# Revit family: P550083-031
name_source: partatom
category: Lighting Fixtures
units: mm (PartAtom-declared; Revit-internal decimal feet)

## family parameters
Cut with Voids When Loaded = No
Host = Face
Light Source = Yes
OmniClass Number = 23.80.70.11.14.17
OmniClass Title = Direct/Indirect
Part Type = Normal
Room Calculation Point = No
Round Connector Dimension = Use Diameter
Shared = Yes

## types (1)
- P550083-031
    Apparent Load = 60 VA
    Assembly Code = D5020200
    Color Filter = 16777215
    Connector Description = Lighting Connector
    Default Elevation = 48 "
    Description = Pawley Collection One-Light Matte Black and Dark Gray Rattan Indoor/Outdoor Hanging Pendant Light
    Dimming Lamp Color Temperature Shift = <None>
    Features = Application: Unite global feel and coastal warmth with the Pawley Collection 1-Light Dark Gray Rattan Coastal Outdoor Hanging Pendant Light ideal for any hallway, stairwell, entryway, kitchen, sitting room, covered patio, or porch.
Styles: Perfect for coastal, global, and transitional style settings.
Finish: The synthetic dark gray rattan frame has a graceful, lattice-like design that gives the fixture charm and depth.
Materials: Constructed from steel to ensure a long product lifespan.
Glass/Shades: A light source diffuses from within the etched glass shade cradled inside the airy basketweave design offering an organic feel.
Bulbs: For ideal illumination, use 1 medium base bulb that is sold separately (100w max - LED/CFL/incandescent). Compatible with dimmable bulbs.
Dimensions: Measures 12-inch diameter by 16-inch height.
Certifications: cETLus damp location listed.
Pairs With: Pairs with a variety of Progress Lighting fixtures.
Warranty: Our 1-Year Limited Warranty guarantees your complete satisfaction with your purchase and includes professional after-sales customer service support.
    Fixture distribution = Direct
    Glass = Paint - Hubbell - White Texture
    Gold = Hubbell - Gold
    Housing Material = Paint - Hubbell - Textured Camera Black
    Lamp = LED/CFL/incandescent
    Load Classification = Lighting
    Manufacturer = Progress Lighting
    Model = P550083-031
    Photometric Web File = generic
    Power Factor = 1
    Product Documentation Link = https://hubbellcdn.com
    Product Link = https://www.hubbell.com
    Tilt Angle = -90.00°
    URL = https://www.hubbell.com
    Voltage = 120 V
    Warranty = 1 year Warranty
    Wattage Comments = 60W
    Watts = 60 W
    Wood = Hubbell - Gray

## geometry (parser evidence)
native form markers: Sweep x1
no freeform markers — native parametric forms only
